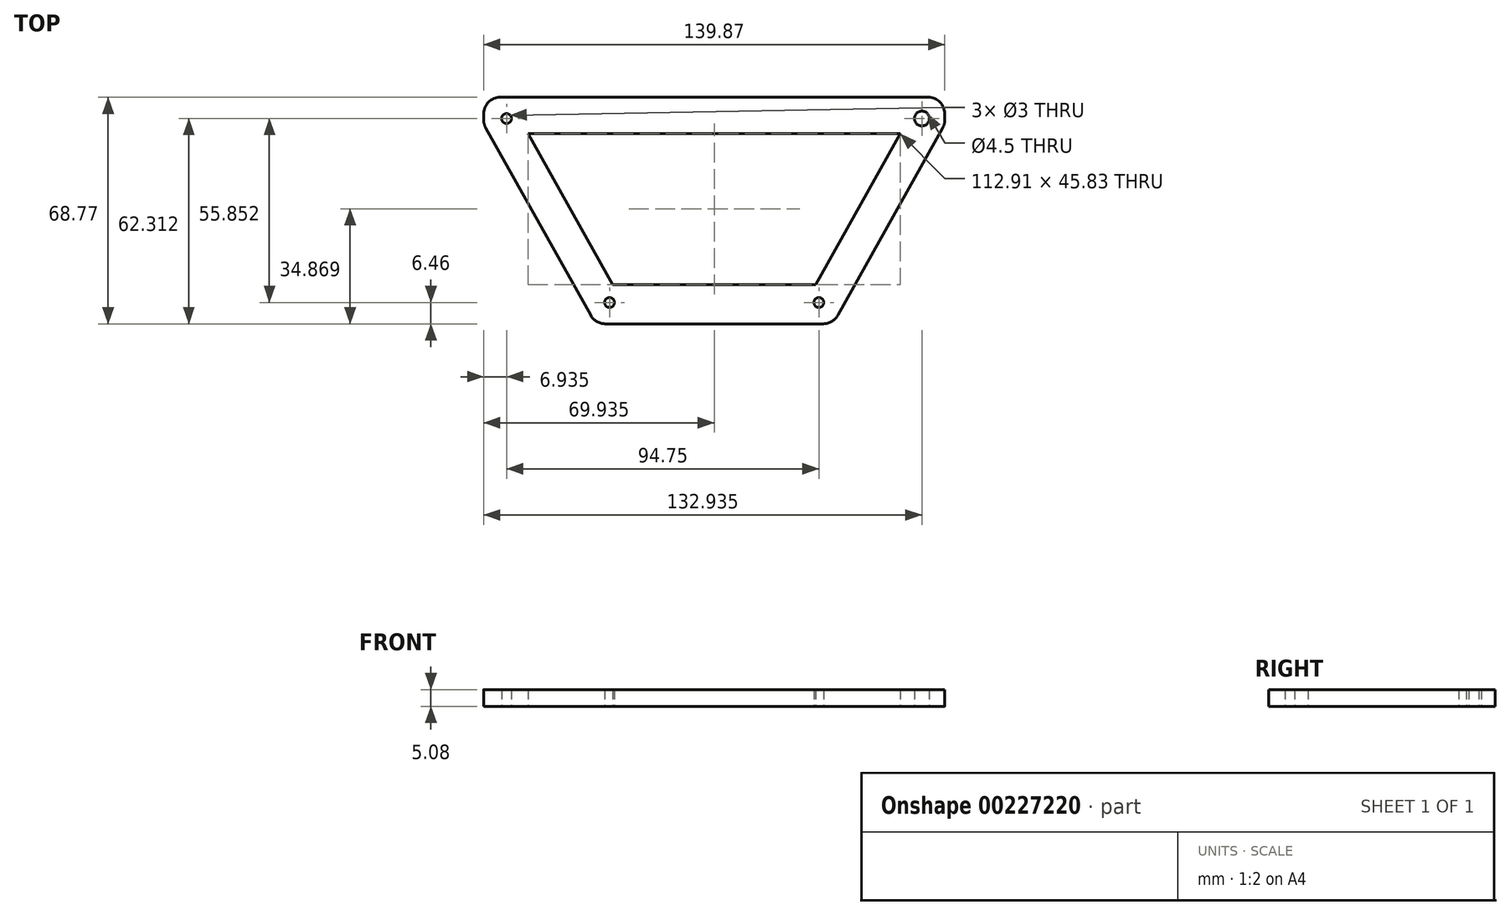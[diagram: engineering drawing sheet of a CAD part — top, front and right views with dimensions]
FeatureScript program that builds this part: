
annotation { "Feature Type Name" : "Feature", "Feature Type Description" : "" }
export const myFeature = defineFeature(function(context is Context, id is Id, definition is map)
    precondition{}
    {
        {
            var Q0;
            Q0=qCreatedBy(makeId("Top.planeOp"),FACE);
            var sketch = newSketch(context, id + "F0", { "sketchPlane" : qUnion([Q0])});
            skCircle(sketch, "E0", {"center": v(-53.16, 55.85) * mm, "radius": 1.5 * mm});
            skCircle(sketch, "E1", {"center": v(-21.91, 0) * mm, "radius": 1.5 * mm});
            skLineSegment(sketch, "E2", {"start": v(-21.91, 0) * mm, "end": v(9.84, 0) * mm});
            skLineSegment(sketch, "E3", {"start": v(-21.91, 0) * mm, "end": v(-53.16, 55.85) * mm});
            skLineSegment(sketch, "E4", {"start": v(-53.16, 55.85) * mm, "end": v(9.84, 55.85) * mm});
            skPoint(sketch, "E5.middle", {"position": v(9.84, 55.85) * mm});
            skPoint(sketch, "E6.middle", {"position": v(9.84, 0) * mm});
            skLineSegment(sketch, "E7", {"start": v(9.84, 0) * mm, "end": v(9.84, 55.85) * mm});
            skLineSegment(sketch, "E8.bottom", {"start": v(79.77, 62.3) * mm, "end": v(-60.1, 62.3) * mm});
            skLineSegment(sketch, "E8.top", {"start": v(79.77, -6.46) * mm, "end": v(-60.1, -6.46) * mm});
            skLineSegment(sketch, "E8.left", {"start": v(79.77, 62.3) * mm, "end": v(79.77, -6.46) * mm});
            skLineSegment(sketch, "E8.right", {"start": v(-60.1, 62.3) * mm, "end": v(-60.1, -6.46) * mm});
            skPoint(sketch, "E8.middle", {"position": v(9.84, 27.93) * mm});
            skLineSegment(sketch, "E9", {"start": v(-60.1, 54.12) * mm, "end": v(-26.2, -6.46) * mm});
            skLineSegment(sketch, "E10.MirrorCS", {"start": v(72.84, 55.85) * mm, "end": v(9.84, 55.85) * mm});
            skCircle(sketch, "E11.MirrorC", {"center": v(72.84, 55.85) * mm, "radius": 1.5 * mm});
            skLineSegment(sketch, "E12.MirrorCS", {"start": v(41.59, 0) * mm, "end": v(72.84, 55.85) * mm});
            skLineSegment(sketch, "E13.MirrorCS", {"start": v(41.59, 0) * mm, "end": v(9.84, 0) * mm});
            skLineSegment(sketch, "E14.MirrorCS", {"start": v(79.77, 54.12) * mm, "end": v(45.87, -6.46) * mm});
            skCircle(sketch, "E15.MirrorC", {"center": v(41.59, 0) * mm, "radius": 1.5 * mm});
            skLineSegment(sketch, "E16", {"start": v(-17.9, 0) * mm, "end": v(-49.15, 55.85) * mm});
            skLineSegment(sketch, "E17", {"start": v(-50.63, 51.33) * mm, "end": v(9.84, 51.33) * mm});
            skLineSegment(sketch, "E18", {"start": v(9.84, 5.5) * mm, "end": v(-24.99, 5.5) * mm});
            skLineSegment(sketch, "E19.MirrorCS", {"start": v(70.3, 51.33) * mm, "end": v(9.84, 51.33) * mm});
            skLineSegment(sketch, "E20.MirrorCS", {"start": v(37.57, 0) * mm, "end": v(68.82, 55.85) * mm});
            skLineSegment(sketch, "E21.MirrorCS", {"start": v(9.84, 5.5) * mm, "end": v(44.66, 5.5) * mm});
            skLineSegment(sketch, "E22.bottom", {"start": v(73.94, 56.95) * mm, "end": v(71.74, 56.95) * mm});
            skLineSegment(sketch, "E22.top", {"start": v(73.94, 54.75) * mm, "end": v(71.74, 54.75) * mm});
            skLineSegment(sketch, "E22.left", {"start": v(73.94, 56.95) * mm, "end": v(73.94, 54.75) * mm});
            skLineSegment(sketch, "E22.right", {"start": v(71.74, 56.95) * mm, "end": v(71.74, 54.75) * mm});
            skCircle(sketch, "E23", {"center": v(72.84, 55.85) * mm, "radius": 2.25 * mm});
            skSolve(sketch);
        }
        {
            var Q0;
            {var subQ1=sQuery(id+"F0.wireOp",EDGE,"E2");var subQ3=sQuery(id+"F0.wireOp",EDGE,"E16");var subQ4=makeQuery(id+"F0.imprint","INTERSECT",VERTEX,{"derivedFrom":[subQ1,subQ3]});Q0=makeQuery(id+"F0.imprint","IMPRINT",FACE,{"disambiguationData":[TD([[makeQuery(id+"F0.imprint","IMPRINT",EDGE,{"disambiguationData":[TD([[subQ4,-1.0]])],"derivedFrom":subQ3}),-1.0]])]});}
            var Q1;
            {var subQ1=sQuery(id+"F0.wireOp",EDGE,"E4");var subQ3=sQuery(id+"F0.wireOp",EDGE,"E16");var subQ4=makeQuery(id+"F0.imprint","INTERSECT",VERTEX,{"derivedFrom":[subQ1,subQ3]});Q1=makeQuery(id+"F0.imprint","IMPRINT",FACE,{"disambiguationData":[TD([[makeQuery(id+"F0.imprint","IMPRINT",EDGE,{"disambiguationData":[TD([[subQ4,1.0]])],"derivedFrom":subQ3}),-1.0]])]});}
            var Q2;
            {var subQ16=sQuery(id+"F0.wireOp",EDGE,"E8.bottom");Q2=makeQuery(id+"F0.imprint","IMPRINT",FACE,{"disambiguationData":[TD([[makeQuery(id+"F0.imprint","IMPRINT",EDGE,{"derivedFrom":subQ16}),1.0]])]});}
            var Q3;
            {var subQ0=sQuery(id+"F0.wireOp",EDGE,"E13.MirrorCS");var subQ5=sQuery(id+"F0.wireOp",EDGE,"E20.MirrorCS");var subQ7=makeQuery(id+"F0.imprint","INTERSECT",VERTEX,{"derivedFrom":[subQ0,subQ5]});Q3=makeQuery(id+"F0.imprint","IMPRINT",FACE,{"disambiguationData":[TD([[makeQuery(id+"F0.imprint","IMPRINT",EDGE,{"disambiguationData":[TD([[subQ7,-1.0]])],"derivedFrom":subQ5}),1.0]])]});}
            var Q4;
            {var subQ0=sQuery(id+"F0.wireOp",EDGE,"E10.MirrorCS");var subQ5=sQuery(id+"F0.wireOp",EDGE,"E20.MirrorCS");var subQ6=makeQuery(id+"F0.imprint","INTERSECT",VERTEX,{"derivedFrom":[subQ0,subQ5]});Q4=makeQuery(id+"F0.imprint","IMPRINT",FACE,{"disambiguationData":[TD([[makeQuery(id+"F0.imprint","IMPRINT",EDGE,{"disambiguationData":[TD([[subQ6,1.0]])],"derivedFrom":subQ5}),1.0]])]});}
            var Q5;
            {var subQ0=sQuery(id+"F0.wireOp",EDGE,"E17");var subQ1=sQuery(id+"F0.wireOp",EDGE,"E3");var subQ2=makeQuery(id+"F0.imprint","INTERSECT",VERTEX,{"derivedFrom":[subQ1,subQ0]});Q5=makeQuery(id+"F0.imprint","IMPRINT",FACE,{"disambiguationData":[TD([[makeQuery(id+"F0.imprint","IMPRINT",EDGE,{"disambiguationData":[TD([[subQ2,1.0]])],"derivedFrom":subQ1}),-1.0]])]});}
            var Q6;
            {var subQ3=sQuery(id+"F0.wireOp",EDGE,"E0");var subQ6=sQuery(id+"F0.wireOp",EDGE,"E3");var subQ9=makeQuery(id+"F0.imprint","INTERSECT",VERTEX,{"derivedFrom":[subQ3,subQ6]});Q6=makeQuery(id+"F0.imprint","IMPRINT",FACE,{"disambiguationData":[TD([[makeQuery(id+"F0.imprint","IMPRINT",EDGE,{"disambiguationData":[TD([[subQ9,-1.0]])],"derivedFrom":subQ3}),-1.0]])]});}
            var Q7;
            {var subQ0=sQuery(id+"F0.wireOp",EDGE,"E19.MirrorCS");var subQ1=sQuery(id+"F0.wireOp",EDGE,"E12.MirrorCS");var subQ2=makeQuery(id+"F0.imprint","INTERSECT",VERTEX,{"derivedFrom":[subQ1,subQ0]});Q7=makeQuery(id+"F0.imprint","IMPRINT",FACE,{"disambiguationData":[TD([[makeQuery(id+"F0.imprint","IMPRINT",EDGE,{"disambiguationData":[TD([[subQ2,1.0]])],"derivedFrom":subQ1}),1.0]])]});}
            var Q8;
            {var subQ3=sQuery(id+"F0.wireOp",EDGE,"E21.MirrorCS");var subQ6=sQuery(id+"F0.wireOp",EDGE,"E12.MirrorCS");var subQ9=makeQuery(id+"F0.imprint","INTERSECT",VERTEX,{"derivedFrom":[subQ6,subQ3]});Q8=makeQuery(id+"F0.imprint","IMPRINT",FACE,{"disambiguationData":[TD([[makeQuery(id+"F0.imprint","IMPRINT",EDGE,{"disambiguationData":[TD([[subQ9,1.0]])],"derivedFrom":subQ6}),1.0]])]});}
            var Q9;
            {var subQ1=sQuery(id+"F0.wireOp",EDGE,"E2");var subQ7=sQuery(id+"F0.wireOp",EDGE,"E1");var subQ9=makeQuery(id+"F0.imprint","INTERSECT",VERTEX,{"derivedFrom":[subQ7,subQ1]});Q9=makeQuery(id+"F0.imprint","IMPRINT",FACE,{"disambiguationData":[TD([[makeQuery(id+"F0.imprint","IMPRINT",EDGE,{"disambiguationData":[TD([[subQ9,-1.0]])],"derivedFrom":subQ7}),-1.0]])]});}
            var Q10;
            {var subQ3=sQuery(id+"F0.wireOp",EDGE,"E20.MirrorCS");var subQ5=sQuery(id+"F0.wireOp",EDGE,"E10.MirrorCS");var subQ6=makeQuery(id+"F0.imprint","INTERSECT",VERTEX,{"derivedFrom":[subQ5,subQ3]});Q10=makeQuery(id+"F0.imprint","IMPRINT",FACE,{"disambiguationData":[TD([[makeQuery(id+"F0.imprint","IMPRINT",EDGE,{"disambiguationData":[TD([[subQ6,1.0]])],"derivedFrom":subQ5}),1.0]])]});}
            extrude(context, id + "F1", {"entities" : qUnion([Q0, Q1, Q2, Q3, Q4, Q5, Q6, Q7, Q8, Q9, Q10]), "depth" : 5.08 * mm});
        }
        {
            var Q0;
            Q0=makeQuery(id+"F1.opExtrude","SWEPT_EDGE",EDGE,{"disambiguationData":[OSD([sQuery(id+"F0.wireOp",EDGE,"E8.bottom"),sQuery(id+"F0.wireOp",EDGE,"E8.right")])]});
            var Q1;
            Q1=makeQuery(id+"F1.opExtrude","SWEPT_EDGE",EDGE,{"disambiguationData":[OSD([sQuery(id+"F0.wireOp",EDGE,"E8.right"),sQuery(id+"F0.wireOp",EDGE,"E9")])]});
            var Q2;
            Q2=makeQuery(id+"F1.opExtrude","SWEPT_EDGE",EDGE,{"disambiguationData":[OSD([sQuery(id+"F0.wireOp",EDGE,"E8.bottom"),sQuery(id+"F0.wireOp",EDGE,"E8.left")])]});
            var Q3;
            Q3=makeQuery(id+"F1.opExtrude","SWEPT_EDGE",EDGE,{"disambiguationData":[OSD([sQuery(id+"F0.wireOp",EDGE,"E8.left"),sQuery(id+"F0.wireOp",EDGE,"E14.MirrorCS")])]});
            var Q4;
            Q4=makeQuery(id+"F1.opExtrude","SWEPT_EDGE",EDGE,{"disambiguationData":[OSD([sQuery(id+"F0.wireOp",EDGE,"E8.top"),sQuery(id+"F0.wireOp",EDGE,"E14.MirrorCS")])]});
            var Q5;
            Q5=makeQuery(id+"F1.opExtrude","SWEPT_EDGE",EDGE,{"disambiguationData":[OSD([sQuery(id+"F0.wireOp",EDGE,"E8.top"),sQuery(id+"F0.wireOp",EDGE,"E9")])]});
            fillet(context, id + "F2", {"entities" : qUnion([Q0, Q1, Q2, Q3, Q4, Q5]), "radius" : 5 * mm, "tangentPropagation" : true, "allowEdgeOverflow" : false});
        }
    });
